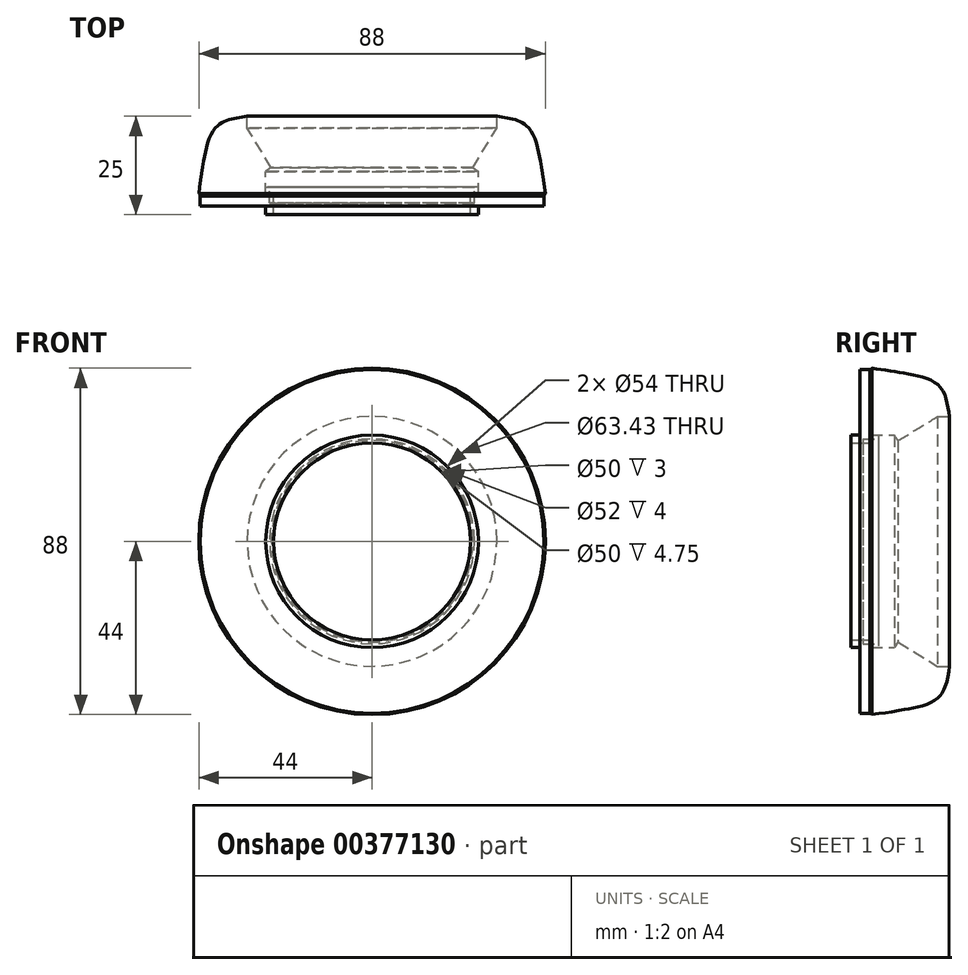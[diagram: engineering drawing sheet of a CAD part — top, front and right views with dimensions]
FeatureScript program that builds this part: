
annotation { "Feature Type Name" : "Feature", "Feature Type Description" : "" }
export const myFeature = defineFeature(function(context is Context, id is Id, definition is map)
    precondition{}
    {
        {
            var Q0;
            Q0=qCreatedBy(makeId("Right.planeOp"),FACE);
            var sketch = newSketch(context, id + "F0", { "sketchPlane" : qUnion([Q0])});
            skLineSegment(sketch, "E0", {"start": v(24.66, 0) * mm, "end": v(24.66, 44.5) * mm, "construction": true});
            skLineSegment(sketch, "E1", {"start": v(24.66, 44.5) * mm, "end": v(0, 44.5) * mm, "construction": true});
            skLineSegment(sketch, "E2.left", {"start": v(24.66, 30) * mm, "end": v(24.66, 0) * mm});
            skLineSegment(sketch, "E3.top", {"start": v(3.5, 27) * mm, "end": v(7.5, 27) * mm});
            skLineSegment(sketch, "E3.left", {"start": v(3.5, 0) * mm, "end": v(3.5, 27) * mm});
            skLineSegment(sketch, "E3.right", {"start": v(7.5, 25) * mm, "end": v(7.5, 27) * mm});
            skLineSegment(sketch, "E4", {"start": v(7.5, 25) * mm, "end": v(10, 23.5) * mm});
            skFitSpline(sketch, "E5", {"points": [v(10, 23.5) * mm, v(18.5, 0) * mm], "startDerivative": vector(10.8, -12.83) * mm, "endDerivative": vector(0.5, -36.07) * mm});
            skLineSegment(sketch, "E6", {"start": v(0, 27) * mm, "end": v(0.5, 27) * mm});
            skLineSegment(sketch, "E7", {"start": v(0.5, 27) * mm, "end": v(0.5, 0) * mm});
            skLineSegment(sketch, "E8", {"start": v(0.5, 27) * mm, "end": v(3.5, 27) * mm, "construction": true});
            skLineSegment(sketch, "E9", {"start": v(6.93, 27) * mm, "end": v(6.93, 25) * mm, "construction": true});
            skLineSegment(sketch, "E10", {"start": v(7.5, 25) * mm, "end": v(6.93, 25) * mm, "construction": true});
            skFitSpline(sketch, "E11", {"points": [v(6.93, 25) * mm, v(1.5, 0) * mm], "startDerivative": vector(-10.3, -10.3) * mm, "endDerivative": vector(-0.16, -38) * mm, "construction": true});
            skLineSegment(sketch, "E12", {"start": v(0, 27) * mm, "end": v(0, 0) * mm});
            skLineSegment(sketch, "E13", {"start": v(0, 0) * mm, "end": v(0.5, 0) * mm});
            skLineSegment(sketch, "E14.bottom", {"start": v(19.5, 32.5) * mm, "end": v(20.5, 32.5) * mm});
            skLineSegment(sketch, "E14.top", {"start": v(19.5, 0) * mm, "end": v(20.5, 0) * mm});
            skLineSegment(sketch, "E14.left", {"start": v(19.5, 32.5) * mm, "end": v(19.5, 0) * mm});
            skLineSegment(sketch, "E14.right", {"start": v(20.5, 32.5) * mm, "end": v(20.5, 0) * mm});
            skLineSegment(sketch, "E15", {"start": v(7.5, 25) * mm, "end": v(19.5, 32.5) * mm});
            skLineSegment(sketch, "E16", {"start": v(20.5, 31.72) * mm, "end": v(21.5, 31.72) * mm});
            skLineSegment(sketch, "E17", {"start": v(3.5, 0) * mm, "end": v(18.5, 0) * mm});
            skLineSegment(sketch, "E18", {"start": v(3.5, 0) * mm, "end": v(1.5, 0) * mm, "construction": true});
            skLineSegment(sketch, "E19", {"start": v(0, 44.5) * mm, "end": v(0, 27) * mm, "construction": true});
            skLineSegment(sketch, "E20", {"start": v(0, 43.65) * mm, "end": v(1.25, 43.65) * mm, "construction": true});
            skLineSegment(sketch, "E21", {"start": v(1.25, 43.65) * mm, "end": v(1.25, 39) * mm});
            skLineSegment(sketch, "E22", {"start": v(1.25, 39) * mm, "end": v(0, 39) * mm, "construction": true});
            skLineSegment(sketch, "E23", {"start": v(1.25, 43.65) * mm, "end": v(1.75, 43.65) * mm, "construction": true});
            skLineSegment(sketch, "E24", {"start": v(1.75, 43.65) * mm, "end": v(1.75, 39) * mm, "construction": true});
            skLineSegment(sketch, "E25", {"start": v(1.75, 39) * mm, "end": v(1.25, 39) * mm});
            skLineSegment(sketch, "E26", {"start": v(1.5, 43.65) * mm, "end": v(1.85, 44) * mm});
            skFitSpline(sketch, "E27", {"points": [v(1.85, 44) * mm, v(21.5, 31.72) * mm], "startDerivative": vector(27.86, -4.33) * mm, "endDerivative": vector(7.5, -23.03) * mm});
            skLineSegment(sketch, "E28", {"start": v(1.5, 43.65) * mm, "end": v(1.75, 43.65) * mm});
            skFitSpline(sketch, "E29.0", {"points": [v(1.55, 42.02) * mm, v(3.8, 41.67) * mm, v(8.1, 40.77) * mm, v(12.58, 38.96) * mm, v(15.46, 37.06) * mm, v(17.25, 35.4) * mm, v(18.65, 33.45) * mm, v(19.33, 31.93) * mm, v(19.6, 31.1) * mm]});
            skLineSegment(sketch, "E30", {"start": v(1.75, 43.65) * mm, "end": v(1.75, 42) * mm});
            skLineSegment(sketch, "E31.0", {"start": v(10.13, 29) * mm, "end": v(18.19, 34.04) * mm});
            skLineSegment(sketch, "E32", {"start": v(1.75, 39) * mm, "end": v(1.75, 27) * mm, "construction": true});
            skLineSegment(sketch, "E33", {"start": v(1.75, 29) * mm, "end": v(10.13, 29) * mm});
            skLineSegment(sketch, "E34", {"start": v(1.75, 29) * mm, "end": v(1.75, 27) * mm});
            skLineSegment(sketch, "E35", {"start": v(1.75, 27) * mm, "end": v(3.5, 27) * mm});
            skLineSegment(sketch, "E36", {"start": v(0.5, 0) * mm, "end": v(-42.58, 0) * mm, "construction": true});
            skLineSegment(sketch, "E37", {"start": v(1.25, 39) * mm, "end": v(1.75, 39) * mm});
            skLineSegment(sketch, "E38", {"start": v(1.25, 43.65) * mm, "end": v(-1.25, 43.65) * mm});
            skLineSegment(sketch, "E39", {"start": v(1.75, 39) * mm, "end": v(1.75, 27) * mm});
            skLineSegment(sketch, "E40", {"start": v(3.5, 25) * mm, "end": v(0.5, 25) * mm});
            skLineSegment(sketch, "E41", {"start": v(0.5, 25) * mm, "end": v(0.5, 27) * mm});
            skLineSegment(sketch, "E42", {"start": v(0.5, 27) * mm, "end": v(-0.5, 27) * mm});
            skLineSegment(sketch, "E43", {"start": v(-1.25, 43.65) * mm, "end": v(-1.25, 39) * mm});
            skLineSegment(sketch, "E44", {"start": v(-1.25, 39) * mm, "end": v(-0.5, 39) * mm});
            skLineSegment(sketch, "E45", {"start": v(-0.5, 39) * mm, "end": v(-0.5, 27) * mm});
            skLineSegment(sketch, "E46", {"start": v(-0.5, 39) * mm, "end": v(0, 39) * mm, "construction": true});
            skLineSegment(sketch, "E47", {"start": v(0, 26.41) * mm, "end": v(0.5, 26.41) * mm, "construction": true});
            skLineSegment(sketch, "E48", {"start": v(-0.5, 27.32) * mm, "end": v(0, 27.32) * mm, "construction": true});
            skLineSegment(sketch, "E49.bottom", {"start": v(1.25, 43.65) * mm, "end": v(1.75, 43.65) * mm});
            skLineSegment(sketch, "E49.right", {"start": v(1.75, 43.65) * mm, "end": v(1.75, 39) * mm});
            skLineSegment(sketch, "E50", {"start": v(-0.5, 39) * mm, "end": v(-1.75, 39) * mm});
            skLineSegment(sketch, "E51", {"start": v(-1.75, 39) * mm, "end": v(-1.75, 27) * mm});
            skLineSegment(sketch, "E52", {"start": v(-1.75, 27) * mm, "end": v(-3.5, 27) * mm});
            skLineSegment(sketch, "E53", {"start": v(-3.5, 27) * mm, "end": v(-3.5, 25) * mm});
            skLineSegment(sketch, "E54", {"start": v(-3.5, 25) * mm, "end": v(-0.5, 25) * mm});
            skLineSegment(sketch, "E55", {"start": v(-0.5, 25) * mm, "end": v(-0.5, 27) * mm});
            skLineSegment(sketch, "E56", {"start": v(0, 29.76) * mm, "end": v(1.75, 29.76) * mm, "construction": true});
            skLineSegment(sketch, "E57", {"start": v(0, 29.05) * mm, "end": v(-1.75, 29.05) * mm, "construction": true});
            skLineSegment(sketch, "E58", {"start": v(-1.75, 27) * mm, "end": v(-0.5, 27) * mm, "construction": true});
            skLineSegment(sketch, "E59", {"start": v(-0.5, 25) * mm, "end": v(0.5, 25) * mm, "construction": true});
            skLineSegment(sketch, "E60.bottom", {"start": v(-0.5, 27) * mm, "end": v(-1, 27) * mm});
            skLineSegment(sketch, "E60.top", {"start": v(-0.5, 25) * mm, "end": v(-1, 25) * mm});
            skLineSegment(sketch, "E60.left", {"start": v(-0.5, 27) * mm, "end": v(-0.5, 25) * mm});
            skLineSegment(sketch, "E60.right", {"start": v(-1, 27) * mm, "end": v(-1, 25) * mm});
            skLineSegment(sketch, "E61.bottom", {"start": v(0.5, 27) * mm, "end": v(1, 27) * mm});
            skLineSegment(sketch, "E61.top", {"start": v(0.5, 25) * mm, "end": v(1, 25) * mm});
            skLineSegment(sketch, "E61.left", {"start": v(0.5, 27) * mm, "end": v(0.5, 25) * mm});
            skLineSegment(sketch, "E61.right", {"start": v(1, 27) * mm, "end": v(1, 25) * mm});
            skLineSegment(sketch, "E62", {"start": v(0.5, 26) * mm, "end": v(1, 26) * mm, "construction": true});
            skLineSegment(sketch, "E63", {"start": v(-0.5, 26) * mm, "end": v(-1, 26) * mm, "construction": true});
            skSolve(sketch);
        }
        {
            var Q0;
            Q0=qCreatedBy(makeId("Right.planeOp"),FACE);
            var sketch = newSketch(context, id + "F1", { "sketchPlane" : qUnion([Q0])});
            skLineSegment(sketch, "E64", {"start": v(1.25, 43.65) * mm, "end": v(1.25, 27) * mm});
            skLineSegment(sketch, "E65", {"start": v(1.25, 27) * mm, "end": v(3.5, 27) * mm});
            skLineSegment(sketch, "E66", {"start": v(3.5, 27) * mm, "end": v(3.5, 26) * mm});
            skLineSegment(sketch, "E67", {"start": v(1.25, 43.65) * mm, "end": v(-1.25, 43.65) * mm});
            skLineSegment(sketch, "E68", {"start": v(-1.25, 43.65) * mm, "end": v(-1.25, 27) * mm});
            skLineSegment(sketch, "E69", {"start": v(-1.25, 27) * mm, "end": v(-3.5, 27) * mm});
            skLineSegment(sketch, "E70", {"start": v(-3.5, 27) * mm, "end": v(-3.5, 25) * mm});
            skLineSegment(sketch, "E71", {"start": v(-3.5, 25) * mm, "end": v(-0.5, 25) * mm});
            skLineSegment(sketch, "E72", {"start": v(-0.5, 25) * mm, "end": v(-0.5, 26) * mm});
            skLineSegment(sketch, "E73", {"start": v(-0.5, 26) * mm, "end": v(3.5, 26) * mm});
            skLineSegment(sketch, "E74", {"start": v(0, 42.6) * mm, "end": v(1.25, 42.6) * mm, "construction": true});
            skLineSegment(sketch, "E75", {"start": v(0, 42.06) * mm, "end": v(-1.25, 42.06) * mm, "construction": true});
            skFitSpline(sketch, "E76.0", {"points": [v(1.85, 44) * mm, v(11.14, 42.56) * mm, v(19, 39.4) * mm, v(21.5, 31.72) * mm]});
            skLineSegment(sketch, "E77", {"start": v(1.85, 44) * mm, "end": v(1.5, 43.65) * mm});
            skLineSegment(sketch, "E78", {"start": v(1.5, 43.65) * mm, "end": v(1.5, 27) * mm});
            skLineSegment(sketch, "E79", {"start": v(1.5, 27) * mm, "end": v(7.5, 27) * mm});
            skLineSegment(sketch, "E80", {"start": v(21.5, 31.72) * mm, "end": v(18.5, 31.72) * mm});
            skLineSegment(sketch, "E81", {"start": v(18.5, 31.72) * mm, "end": v(7.5, 25) * mm});
            skLineSegment(sketch, "E82", {"start": v(7.5, 25) * mm, "end": v(7.5, 27) * mm});
            skLineSegment(sketch, "E83.bottom", {"start": v(1.25, 43.65) * mm, "end": v(1.5, 43.65) * mm});
            skLineSegment(sketch, "E83.top", {"start": v(1.25, 27) * mm, "end": v(1.5, 27) * mm});
            skLineSegment(sketch, "E84.bottom", {"start": v(18.5, 31.72) * mm, "end": v(20.5, 31.72) * mm});
            skLineSegment(sketch, "E84.top", {"start": v(18.5, 0) * mm, "end": v(20.5, 0) * mm});
            skLineSegment(sketch, "E84.left", {"start": v(18.5, 31.72) * mm, "end": v(18.5, 0) * mm});
            skLineSegment(sketch, "E84.right", {"start": v(20.5, 31.72) * mm, "end": v(20.5, 0) * mm});
            skLineSegment(sketch, "E85", {"start": v(0, 0) * mm, "end": v(-10.97, 0) * mm});
            skLineSegment(sketch, "E86", {"start": v(7.5, 27) * mm, "end": v(8.48, 25.6) * mm});
            skSolve(sketch);
        }
        {
            var Q0;
            Q0=qCreatedBy(makeId("Right.planeOp"),FACE);
            var sketch = newSketch(context, id + "F2", { "sketchPlane" : qUnion([Q0])});
            skLineSegment(sketch, "E87", {"start": v(-1.25, 43.65) * mm, "end": v(1.25, 43.65) * mm});
            skLineSegment(sketch, "E88", {"start": v(1.25, 43.65) * mm, "end": v(1.25, 27) * mm});
            skLineSegment(sketch, "E89", {"start": v(1.25, 27) * mm, "end": v(3.5, 27) * mm});
            skLineSegment(sketch, "E90", {"start": v(3.5, 27) * mm, "end": v(3.5, 25) * mm});
            skLineSegment(sketch, "E91", {"start": v(3.5, 25) * mm, "end": v(-1.25, 25) * mm});
            skLineSegment(sketch, "E92", {"start": v(-1.25, 25) * mm, "end": v(-1.25, 43.65) * mm});
            skSolve(sketch);
        }
        {
            var Q0;
            {var subQ1=sQuery(id+"F1.wireOp",EDGE,"E66");Q0=makeQuery(id+"F1.imprint","IMPRINT",FACE,{"disambiguationData":[TD([[makeQuery(id+"F1.imprint","IMPRINT",EDGE,{"derivedFrom":subQ1}),-1.0]])]});}
            var Q1;
            Q1=sQuery(id+"F1.wireOp",EDGE,"E85");
            revolve(context, id + "F3", {"entities" : qUnion([Q0]), "axis" : qUnion([Q1]), "revolveType" : RevolveType.FULL});
        }
        {
            var Q0;
            Q0=makeQuery(id+"F1.imprint","IMPRINT",FACE,{"disambiguationData":[TD([[makeQuery(id+"F1.imprint","IMPRINT",EDGE,{"derivedFrom":sQuery(id+"F1.wireOp",EDGE,"E84.bottom")}),-1.0]])]});
            var Q1;
            Q1=makeQuery(id+"F1.imprint","IMPRINT",FACE,{"disambiguationData":[TD([[makeQuery(id+"F1.imprint","IMPRINT",EDGE,{"derivedFrom":sQuery(id+"F1.wireOp",EDGE,"E83.bottom")}),-1.0]])]});
            var Q2;
            Q2=sQuery(id+"F1.wireOp",EDGE,"E85");
            revolve(context, id + "F4", {"entities" : qUnion([Q0, Q1]), "axis" : qUnion([Q2]), "revolveType" : RevolveType.FULL});
        }
        {
            var Q0;
            Q0=makeQuery(id+"F1.imprint","IMPRINT",FACE,{"disambiguationData":[TD([[makeQuery(id+"F1.imprint","IMPRINT",EDGE,{"derivedFrom":sQuery(id+"F1.wireOp",EDGE,"E76.0")}),-1.0]])]});
            var Q1;
            Q1=sQuery(id+"F1.wireOp",EDGE,"E85");
            revolve(context, id + "F5", {"entities" : qUnion([Q0]), "axis" : qUnion([Q1]), "revolveType" : RevolveType.FULL});
        }
        {
            var Q0;
            Q0=makeQuery(id+"F2.imprint","IMPRINT",FACE,{"disambiguationData":[TD([[makeQuery(id+"F2.imprint","IMPRINT",EDGE,{"derivedFrom":sQuery(id+"F2.wireOp",EDGE,"E87")}),-1.0]])]});
            var Q1;
            Q1=sQuery(id+"F1.wireOp",EDGE,"E85");
            revolve(context, id + "F6", {"entities" : qUnion([Q0]), "axis" : qUnion([Q1]), "revolveType" : RevolveType.FULL});
        }
    });
